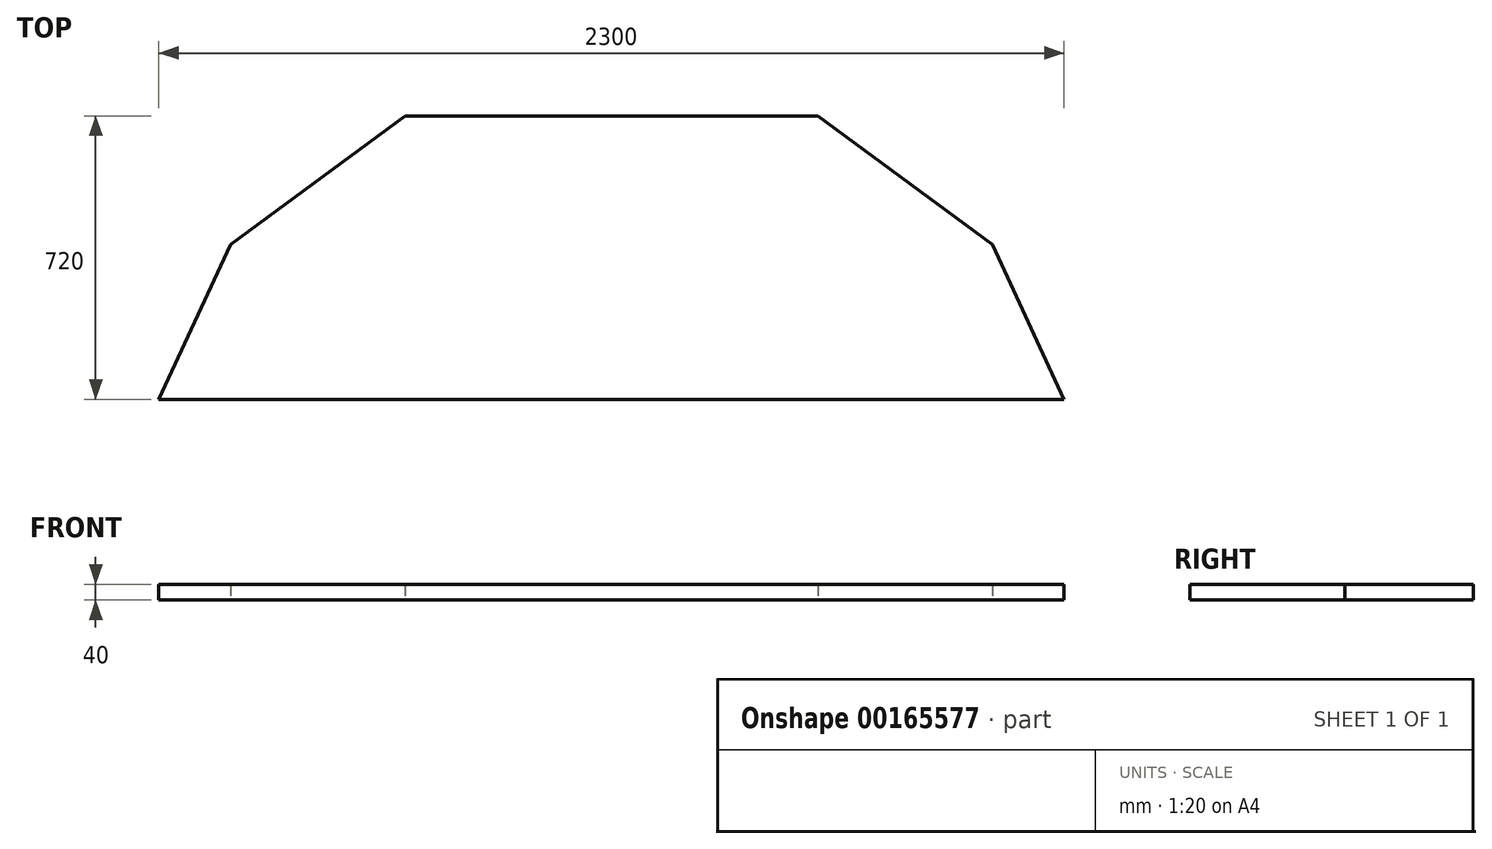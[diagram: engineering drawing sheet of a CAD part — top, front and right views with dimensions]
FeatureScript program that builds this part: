
annotation { "Feature Type Name" : "Feature", "Feature Type Description" : "" }
export const myFeature = defineFeature(function(context is Context, id is Id, definition is map)
    precondition{}
    {
        {
            var Q0;
            Q0=qCreatedBy(makeId("Top.planeOp"),FACE);
            var sketch = newSketch(context, id + "F0", { "sketchPlane" : qUnion([Q0])});
            skLineSegment(sketch, "E0", {"start": v(-1150, -720) * mm, "end": v(1150, -720) * mm});
            skLineSegment(sketch, "E1", {"start": v(1150, -720) * mm, "end": v(967.3, -326.9) * mm});
            skLineSegment(sketch, "E2", {"start": v(967.3, -326.9) * mm, "end": v(525, 0) * mm});
            skLineSegment(sketch, "E3", {"start": v(525, 0) * mm, "end": v(-525, 0) * mm});
            skLineSegment(sketch, "E4", {"start": v(-525, 0) * mm, "end": v(-967.3, -326.9) * mm});
            skLineSegment(sketch, "E5", {"start": v(-967.3, -326.9) * mm, "end": v(-1150, -720) * mm});
            skPoint(sketch, "E6", {"position": v(0, -720) * mm});
            skPoint(sketch, "E7", {"position": v(0, 0) * mm});
            skSolve(sketch);
        }
        {
            var Q0;
            Q0=makeQuery(id+"F0.imprint","IMPRINT",FACE,{"disambiguationData":[TD([[makeQuery(id+"F0.imprint","IMPRINT",EDGE,{"derivedFrom":sQuery(id+"F0.wireOp",EDGE,"E0")}),1.0]])]});
            extrude(context, id + "F1", {"entities" : qUnion([Q0]), "depth" : 40 * mm});
        }
    });
